# Revit family: NLRS_57_AIR_UN_duct-diffuser-wuck-return_LT_sacs
name_source: partatom
category: Air Terminals
units: mm (PartAtom-declared; Revit-internal decimal feet)

## family parameters
Always vertical = Yes
Cut with Voids When Loaded = No
Part Type = Normal
Room Calculation Point = No
Round Connector Dimension = Use Diameter
Shared = No
Work Plane-Based = No

## types (16) — shared parameters
Assembly Code = 57
Description = Grill for round duct, type WUCK (return)
FireRating = 00
IfcDescription = Grill for round duct, type WUCK (return)
IfcExportAs = IfcAirterminal
IfcExportType = Diffuser
IsExternal = No
LoadBearing = No
Model = WUCK
NLRS_C_content_datum_uitgifte = 13-04-2023
NLRS_C_content_provider = Solid Air Climate Solutions
NLRS_C_content_versie = 3.20.01
SACS_Article_Data = WUCK_Data
SACS_Max_Lp_dBA = 28
SACS_Max_Ploss = 15.0 Pa
URL = https://solid-air.nl
zero-valued in all types: Default Elevation

## per-type parameters (varying)
| type | Max Flow | Min Flow | SACS_Factor_LpF1 | SACS_Factor_LpF2 | SACS_Factor_PsF1 | SACS_Factor_PsF2 | SACS_Price_Height | SACS_Price_Width | SACS_Product_Cost |
| 215x65 | 288.0 m³/h | 54.0 m³/h | -109.654145 | 25.486702 | 52.882948 | 2.001157 | 65 mm  [stored 0.213255 ft] | 215 mm | 26 $ |
| 315x65 | 360.0 m³/h | 90.0 m³/h | -119.449886 | 25.72635 | 21.264658 | 2.025068 | 65 mm  [stored 0.213255 ft] | 315 mm  [stored 1.03346 ft] | 29 $ |
| 415x65 | 450.0 m³/h | 108.0 m³/h | -133.182774 | 27.12261 | 24.528757 | 1.905614 | 65 mm  [stored 0.213255 ft] | 415 mm  [stored 1.36155 ft] | 34 $ |
| 515x65 | 450.0 m³/h | 144.0 m³/h | -136.601964 | 26.888521 | 7.065055 | 2.049933 | 65 mm  [stored 0.213255 ft] | 515 mm  [stored 1.68963 ft] | 37 $ |
| 615x65 | 450.0 m³/h | 180.0 m³/h | -135.126343 | 25.992237 | 7.392976 | 1.966979 | 65 mm  [stored 0.213255 ft] | 615 mm  [stored 2.01772 ft] | 41 $ |
| 815x65 | 720.0 m³/h | 216.0 m³/h | 0 | 0 | 0 | 0 | 65 mm  [stored 0.213255 ft] | 815 mm  [stored 2.67388 ft] | 49 $ |
| 215x115 | 450.0 m³/h | 108.0 m³/h | -123.902454 | 25.726251 | 14.017721 | 2.020669 | 115 mm  [stored 0.377297 ft] | 215 mm | 30 $ |
| 315x115 | 720.0 m³/h | 144.0 m³/h | -134.488362 | 26.094501 | 6.66393 | 2.014195 | 115 mm  [stored 0.377297 ft] | 315 mm  [stored 1.03346 ft] | 0 $ |
| 415x115 | 720.0 m³/h | 216.0 m³/h | -140.004625 | 26.020028 | 1.739264 | 2.135714 | 115 mm  [stored 0.377297 ft] | 415 mm  [stored 1.36155 ft] | 42 $ |
| 515x115 | 1440.0 m³/h | 288.0 m³/h | -143.767401 | 25.839645 | 2.78593 | 1.996101 | 115 mm  [stored 0.377297 ft] | 515 mm  [stored 1.68963 ft] | 47 $ |
| 615x115 | 1440.0 m³/h | 360.0 m³/h | -152.057313 | 26.51508 | 2.621395 | 1.954071 | 115 mm  [stored 0.377297 ft] | 615 mm  [stored 2.01772 ft] | 50 $ |
| 815x115 | 1440.0 m³/h | 450.0 m³/h | -155.225643 | 26.044701 | 1.381102 | 1.962847 | 115 mm  [stored 0.377297 ft] | 815 mm  [stored 2.67388 ft] | 60 $ |
| 415x215 | 1800.0 m³/h | 450.0 m³/h | -152.535572 | 25.811326 | 0.992448 | 2.019199 | 215 mm | 415 mm  [stored 1.36155 ft] | 54 $ |
| 515x215 | 2160.0 m³/h | 540.0 m³/h | -160.36588 | 26.210369 | 0.666498 | 2.014833 | 215 mm | 515 mm  [stored 1.68963 ft] | 60 $ |
| 615x215 | 2880.0 m³/h | 720.0 m³/h | -166.503603 | 26.510558 | 0.56954 | 1.988104 | 215 mm | 615 mm  [stored 2.01772 ft] | 70 $ |
| 815x215 | 3600.0 m³/h | 720.0 m³/h | -167.842345 | 25.870086 | 0.35103 | 1.97785 | 215 mm | 815 mm  [stored 2.67388 ft] | 0 $ |

note: [stored X ft] marks values corroborated as IEEE doubles in the binary element streams (Revit-internal decimal feet)

## geometry (parser evidence)
native form markers: Sweep x18
no freeform markers — native parametric forms only
